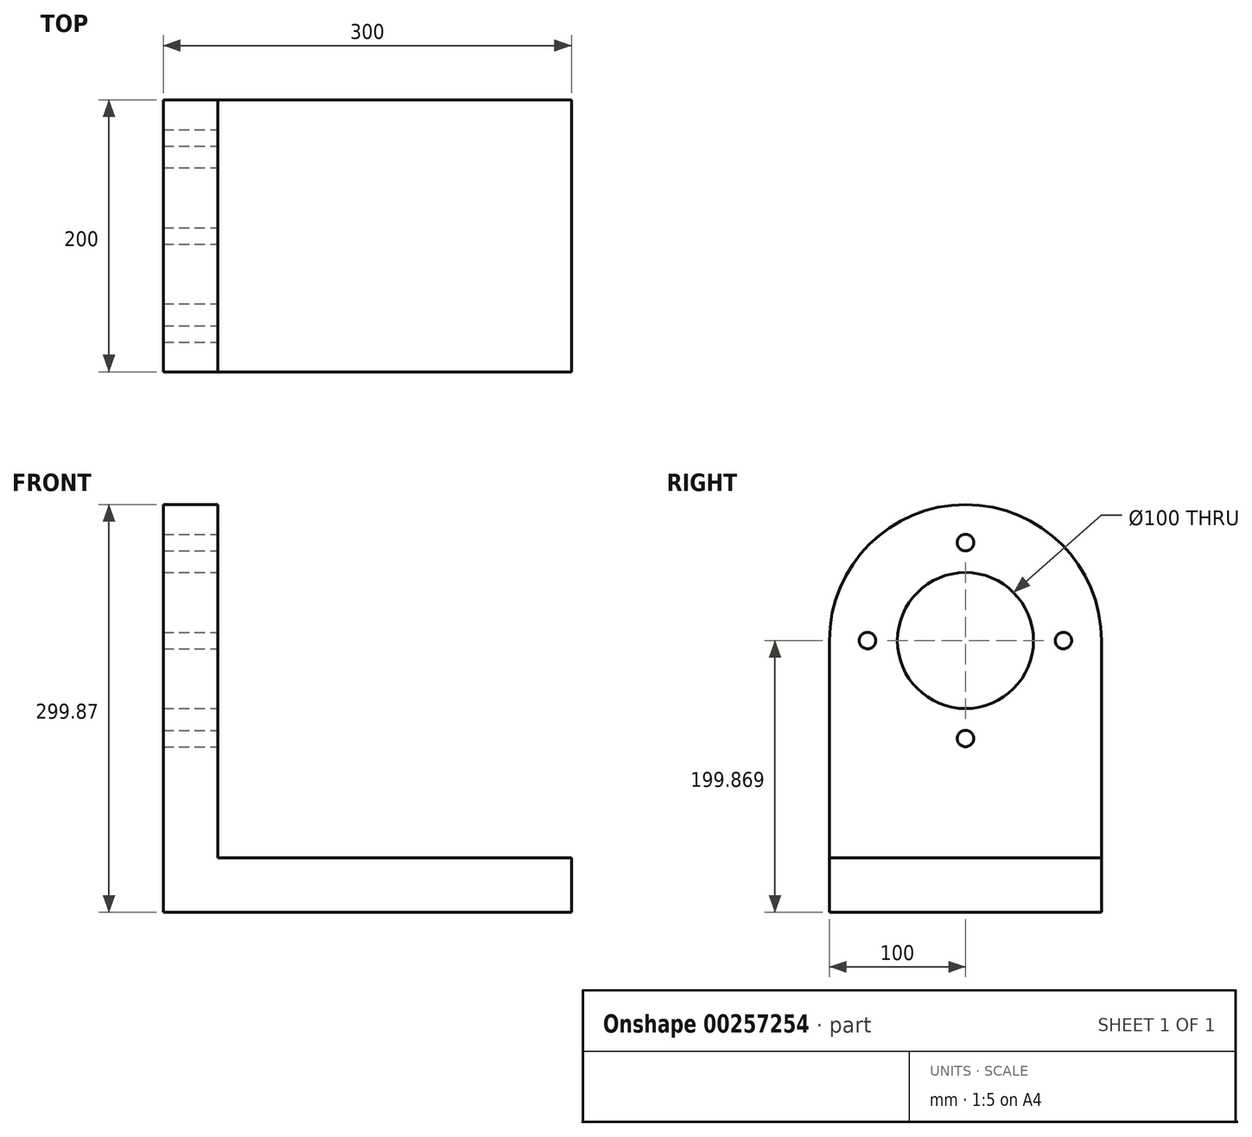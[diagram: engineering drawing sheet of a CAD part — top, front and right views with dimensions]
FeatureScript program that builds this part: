
annotation { "Feature Type Name" : "Feature", "Feature Type Description" : "" }
export const myFeature = defineFeature(function(context is Context, id is Id, definition is map)
    precondition{}
    {
        {
            var Q0;
            Q0=qCreatedBy(makeId("Front.planeOp"),FACE);
            var sketch = newSketch(context, id + "F0", { "sketchPlane" : qUnion([Q0])});
            skLineSegment(sketch, "E0.bottom", {"start": v(-127.04, 0) * mm, "end": v(172.96, 0) * mm});
            skLineSegment(sketch, "E0.top", {"start": v(-127.04, 40) * mm, "end": v(172.96, 40) * mm});
            skLineSegment(sketch, "E0.left", {"start": v(-127.04, 0) * mm, "end": v(-127.04, 40) * mm});
            skLineSegment(sketch, "E0.right", {"start": v(172.96, 0) * mm, "end": v(172.96, 40) * mm});
            skSolve(sketch);
        }
        {
            var Q0;
            Q0=makeQuery(id+"F0.imprint","IMPRINT",FACE,{"disambiguationData":[TD([[makeQuery(id+"F0.imprint","IMPRINT",EDGE,{"derivedFrom":sQuery(id+"F0.wireOp",EDGE,"E0.bottom")}),1.0]])]});
            extrude(context, id + "F1", {"entities" : qUnion([Q0]), "depth" : 200 * mm});
        }
        {
            var Q0;
            Q0=makeQuery(id+"F1.opExtrude","SWEPT_FACE",FACE,{"disambiguationData":[OSD([sQuery(id+"F0.wireOp",EDGE,"E0.top")])]});
            var sketch = newSketch(context, id + "F2", { "sketchPlane" : qUnion([Q0])});
            skLineSegment(sketch, "E1.bottom", {"start": v(-127.04, 0) * mm, "end": v(-87.04, 0) * mm});
            skLineSegment(sketch, "E1.top", {"start": v(-127.04, -200) * mm, "end": v(-87.04, -200) * mm});
            skLineSegment(sketch, "E1.left", {"start": v(-127.04, 0) * mm, "end": v(-127.04, -200) * mm});
            skLineSegment(sketch, "E1.right", {"start": v(-87.04, 0) * mm, "end": v(-87.04, -200) * mm});
            skSolve(sketch);
        }
        {
            var Q0;
            Q0 = qSketchRegion(id + "F2", true);
            extrude(context, id + "F3", {"entities" : qUnion([Q0]), "operationType" : NewBodyOperationType.ADD, "depth" : 260 * mm});
        }
        {
            var Q0;
            Q0=makeQuery(id+"F3.opExtrude","SWEPT_FACE",FACE,{"disambiguationData":[OSD([sQuery(id+"F2.wireOp",EDGE,"E1.right")])]});
            var sketch = newSketch(context, id + "F4", { "sketchPlane" : qUnion([Q0])});
            skCircle(sketch, "E2", {"center": v(-100, 199.87) * mm, "radius": 100 * mm});
            skPoint(sketch, "E2.centerSnap0", {"position": v(-100, 300) * mm});
            skSolve(sketch);
        }
        {
            var Q0;
            {var subQ1=sQuery(id+"F2.wireOp",EDGE,"E1.right");var subQ7=makeQuery(id+"F3.opExtrude","CAP_EDGE",EDGE,{"disambiguationData":[OSD([subQ1])],"isStart":false});Q0=makeQuery(id+"F4.imprint","IMPRINT",FACE,{"disambiguationData":[TD([[makeQuery(id+"F4.imprint","IMPRINT",EDGE,{"derivedFrom":subQ7}),1.0]])]});}
            var Q1;
            {var subQ1=sQuery(id+"F2.wireOp",EDGE,"E1.right");var subQ7=makeQuery(id+"F3.opExtrude","CAP_EDGE",EDGE,{"disambiguationData":[OSD([subQ1])],"isStart":false});Q1=makeQuery(id+"F4.imprint","IMPRINT",FACE,{"disambiguationData":[TD([[makeQuery(id+"F4.imprint","IMPRINT",EDGE,{"derivedFrom":subQ7}),1.0]])]});}
            var Q2;
            {var subQ1=sQuery(id+"F2.wireOp",EDGE,"E1.right");var subQ7=makeQuery(id+"F3.opExtrude","CAP_EDGE",EDGE,{"disambiguationData":[OSD([subQ1])],"isStart":false});Q2=makeQuery(id+"F4.imprint","IMPRINT",FACE,{"disambiguationData":[TD([[makeQuery(id+"F4.imprint","IMPRINT",EDGE,{"derivedFrom":subQ7}),1.0]])]});}
            extrude(context, id + "F5", {"entities" : qUnion([Q0, Q1, Q2]), "operationType" : NewBodyOperationType.REMOVE, "endBound" : BoundingType.THROUGH_ALL, "oppositeDirection" : true, "depth" : 25.4 * mm});
        }
        {
            var Q0;
            Q0=makeQuery(id+"F3.opExtrude","SWEPT_FACE",FACE,{"disambiguationData":[OSD([sQuery(id+"F2.wireOp",EDGE,"E1.right")])]});
            var sketch = newSketch(context, id + "F6", { "sketchPlane" : qUnion([Q0])});
            skCircle(sketch, "E3", {"center": v(-100, 199.87) * mm, "radius": 50 * mm});
            skCircle(sketch, "E4", {"center": v(-100, 199.87) * mm, "radius": 72 * mm, "construction": true});
            skPoint(sketch, "E5", {"position": v(-100, 271.87) * mm});
            skPoint(sketch, "E6", {"position": v(-28, 199.87) * mm});
            skPoint(sketch, "E7", {"position": v(-172, 199.87) * mm});
            skPoint(sketch, "E8", {"position": v(-100, 127.87) * mm});
            skLineSegment(sketch, "E9", {"start": v(-100, 299.87) * mm, "end": v(-100, 199.87) * mm, "construction": true});
            skLineSegment(sketch, "E10", {"start": v(-100, 199.87) * mm, "end": v(-170.71, 270.58) * mm, "construction": true});
            skLineSegment(sketch, "E11", {"start": v(-170.71, 270.58) * mm, "end": v(-170.71, 270.58) * mm});
            skSolve(sketch);
        }
        {
            var Q0;
            Q0 = qSketchRegion(id + "F6", true);
            extrude(context, id + "F7", {"entities" : qUnion([Q0]), "operationType" : NewBodyOperationType.REMOVE, "endBound" : BoundingType.THROUGH_ALL, "oppositeDirection" : true, "depth" : 25.4 * mm});
        }
        {
            var Q0;
            Q0=sQuery(id+"F6.wireOp",VERTEX,"E5");
            var Q1;
            Q1=sQuery(id+"F6.wireOp",VERTEX,"E7");
            var Q2;
            Q2=sQuery(id+"F6.wireOp",VERTEX,"E8");
            var Q3;
            Q3=sQuery(id+"F6.wireOp",VERTEX,"E6");
            var Q4;
            Q4=makeQuery(id+"F1.opExtrude","SWEPT_BODY",BODY,{"disambiguationData":[OSD([sQuery(id+"F0.wireOp",EDGE,"E0.bottom"),sQuery(id+"F0.wireOp",EDGE,"E0.top"),sQuery(id+"F0.wireOp",EDGE,"E0.left"),sQuery(id+"F0.wireOp",EDGE,"E0.right")])]});
            hole(context, id + "F8", {"style" : HoleStyle.SIMPLE, "endStyle" : HoleEndStyle.THROUGH, "standardTappedOrClearance" : lookupTablePath({ "standard" : "ISO", "engagement" : "75%", "pitch" : "2 mm", "size" : "M14", "type" : "Tapped" }), "standardBlindInLast" : lookupTablePath({ "standard" : "ISO", "engagement" : "75%", "pitch" : "2 mm", "size" : "M14", "type" : "Tapped" }), "holeDiameter" : 12.1 * mm, "showTappedDepth" : true, "tappedDepth" : 12.7 * mm, "tapClearance" : 3, "locations" : qUnion([Q0, Q1, Q2, Q3]), "scope" : qUnion([Q4]), "majorDiameter" : 14 * mm});
        }
        {
            var Q0;
            Q0=sQuery(id+"F6.wireOp",VERTEX,"E10.end");
            var Q1;
            Q1=sQuery(id+"F6.wireOp",EDGE,"E10");
            cPlane(context, id + "F9", {"entities" : qUnion([Q0, Q1]), "cplaneType" : CPlaneType.LINE_POINT, "offset" : 25.4 * mm, "width" : 152.4 * mm, "height" : 152.4 * mm});
        }
    });
